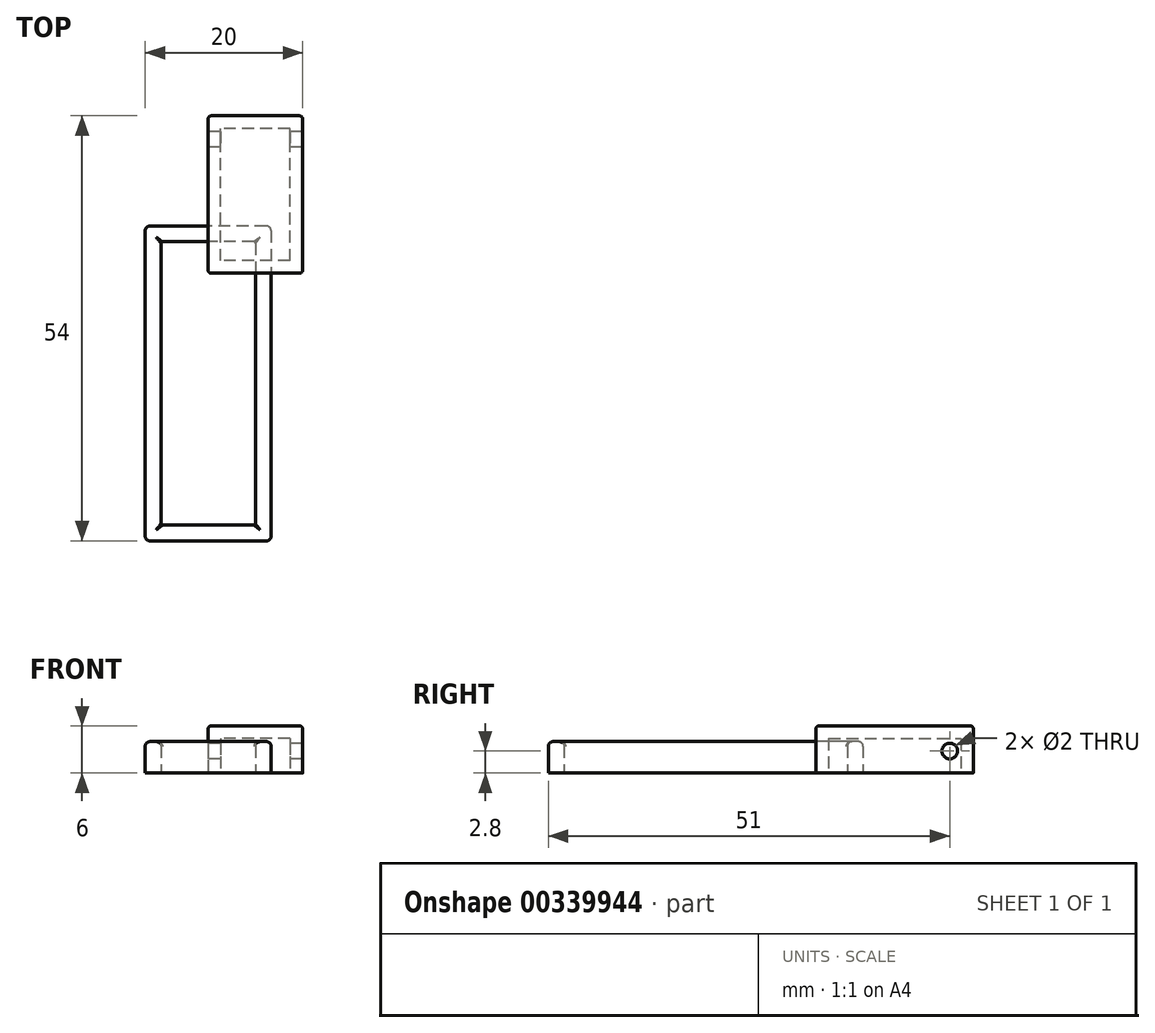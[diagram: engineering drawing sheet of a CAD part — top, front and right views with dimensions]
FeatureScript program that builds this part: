
annotation { "Feature Type Name" : "Feature", "Feature Type Description" : "" }
export const myFeature = defineFeature(function(context is Context, id is Id, definition is map)
    precondition{}
    {
        {
            var Q0;
            Q0=qCreatedBy(makeId("Top.planeOp"),FACE);
            var sketch = newSketch(context, id + "F0", { "sketchPlane" : qUnion([Q0])});
            skLineSegment(sketch, "E0.bottom", {"start": v(6, -10) * mm, "end": v(-6, -10) * mm});
            skLineSegment(sketch, "E0.top", {"start": v(6, 10) * mm, "end": v(-6, 10) * mm});
            skLineSegment(sketch, "E0.left", {"start": v(6, -10) * mm, "end": v(6, 10) * mm});
            skLineSegment(sketch, "E0.right", {"start": v(-6, -10) * mm, "end": v(-6, 10) * mm});
            skPoint(sketch, "E0.middle", {"position": v(0, 0) * mm});
            skSolve(sketch);
        }
        {
            var Q0;
            Q0 = qSketchRegion(id + "F0", true);
            extrude(context, id + "F1", {"entities" : qUnion([Q0]), "depth" : 6 * mm});
        }
        {
            var Q0;
            Q0=makeQuery(id+"F1.opExtrude","CAP_FACE",FACE,{"disambiguationData":[OSD([sQuery(id+"F0.wireOp",EDGE,"E0.bottom"),sQuery(id+"F0.wireOp",EDGE,"E0.top"),sQuery(id+"F0.wireOp",EDGE,"E0.left"),sQuery(id+"F0.wireOp",EDGE,"E0.right")])],"isStart":true});
            shell(context, id + "F2", {"entities" : qUnion([Q0]), "thickness" : 1.6 * mm});
        }
        {
            var Q0;
            Q0=qCreatedBy(makeId("Top.planeOp"),FACE);
            var sketch = newSketch(context, id + "F3", { "sketchPlane" : qUnion([Q0])});
            skLineSegment(sketch, "E1.bottom", {"start": v(2, -4) * mm, "end": v(-14, -4) * mm});
            skLineSegment(sketch, "E1.top", {"start": v(2, -44) * mm, "end": v(-14, -44) * mm});
            skLineSegment(sketch, "E1.left", {"start": v(2, -4) * mm, "end": v(2, -44) * mm});
            skLineSegment(sketch, "E1.right", {"start": v(-14, -4) * mm, "end": v(-14, -44) * mm});
            skPoint(sketch, "E1.middle", {"position": v(-6, -24) * mm});
            skLineSegment(sketch, "E2.0", {"start": v(0, -6) * mm, "end": v(-12, -6) * mm});
            skLineSegment(sketch, "E2.1", {"start": v(0, -6) * mm, "end": v(0, -42) * mm});
            skLineSegment(sketch, "E2.2", {"start": v(0, -42) * mm, "end": v(-12, -42) * mm});
            skLineSegment(sketch, "E2.3", {"start": v(-12, -6) * mm, "end": v(-12, -42) * mm});
            skSolve(sketch);
        }
        {
            var Q0;
            Q0 = qSketchRegion(id + "F3", true);
            extrude(context, id + "F4", {"entities" : qUnion([Q0]), "depth" : 4 * mm, "hasSecondDirection" : true, "secondDirectionOppositeDirection" : false, "secondDirectionDepth" : 0 * mm});
        }
        {
            var Q0;
            Q0=makeQuery(id+"F1.opExtrude","CAP_FACE",FACE,{"disambiguationData":[OSD([sQuery(id+"F0.wireOp",EDGE,"E0.bottom"),sQuery(id+"F0.wireOp",EDGE,"E0.top"),sQuery(id+"F0.wireOp",EDGE,"E0.left"),sQuery(id+"F0.wireOp",EDGE,"E0.right")])],"isStart":false});
            var Q1;
            Q1=makeQuery(id+"F1.opExtrude","SWEPT_EDGE",EDGE,{"disambiguationData":[OSD([sQuery(id+"F0.wireOp",EDGE,"E0.top"),sQuery(id+"F0.wireOp",EDGE,"E0.right")])]});
            var Q2;
            Q2=makeQuery(id+"F1.opExtrude","SWEPT_EDGE",EDGE,{"disambiguationData":[OSD([sQuery(id+"F0.wireOp",EDGE,"E0.bottom"),sQuery(id+"F0.wireOp",EDGE,"E0.right")])]});
            var Q3;
            Q3=makeQuery(id+"F1.opExtrude","SWEPT_EDGE",EDGE,{"disambiguationData":[OSD([sQuery(id+"F0.wireOp",EDGE,"E0.bottom"),sQuery(id+"F0.wireOp",EDGE,"E0.left")])]});
            var Q4;
            Q4=makeQuery(id+"F1.opExtrude","SWEPT_EDGE",EDGE,{"disambiguationData":[OSD([sQuery(id+"F0.wireOp",EDGE,"E0.top"),sQuery(id+"F0.wireOp",EDGE,"E0.left")])]});
            fillet(context, id + "F5", {"entities" : qUnion([Q0, Q1, Q2, Q3, Q4]), "radius" : 0.4 * mm, "tangentPropagation" : true, "allowEdgeOverflow" : false});
        }
        {
            var Q0;
            Q0=makeQuery(id+"F4.opExtrude","CAP_FACE",FACE,{"disambiguationData":[OSD([sQuery(id+"F3.wireOp",EDGE,"E1.bottom"),sQuery(id+"F3.wireOp",EDGE,"E1.top"),sQuery(id+"F3.wireOp",EDGE,"E1.left"),sQuery(id+"F3.wireOp",EDGE,"E1.right"),sQuery(id+"F3.wireOp",EDGE,"E2.0"),sQuery(id+"F3.wireOp",EDGE,"E2.1"),sQuery(id+"F3.wireOp",EDGE,"E2.2"),sQuery(id+"F3.wireOp",EDGE,"E2.3")])],"isStart":false});
            var Q1;
            Q1=makeQuery(id+"F4.opExtrude","SWEPT_EDGE",EDGE,{"disambiguationData":[OSD([sQuery(id+"F3.wireOp",EDGE,"E1.bottom"),sQuery(id+"F3.wireOp",EDGE,"E1.right")])]});
            var Q2;
            Q2=makeQuery(id+"F4.opExtrude","SWEPT_EDGE",EDGE,{"disambiguationData":[OSD([sQuery(id+"F3.wireOp",EDGE,"E1.bottom"),sQuery(id+"F3.wireOp",EDGE,"E1.left")])]});
            var Q3;
            Q3=makeQuery(id+"F4.opExtrude","SWEPT_EDGE",EDGE,{"disambiguationData":[OSD([sQuery(id+"F3.wireOp",EDGE,"E1.top"),sQuery(id+"F3.wireOp",EDGE,"E1.left")])]});
            var Q4;
            Q4=makeQuery(id+"F4.opExtrude","SWEPT_EDGE",EDGE,{"disambiguationData":[OSD([sQuery(id+"F3.wireOp",EDGE,"E1.top"),sQuery(id+"F3.wireOp",EDGE,"E1.right")])]});
            fillet(context, id + "F6", {"entities" : qUnion([Q0, Q1, Q2, Q3, Q4]), "radius" : 0.6 * mm, "tangentPropagation" : true, "allowEdgeOverflow" : false});
        }
        {
            var Q0;
            Q0=makeQuery(id+"F4.opExtrude","SWEPT_EDGE",EDGE,{"disambiguationData":[OSD([sQuery(id+"F3.wireOp",EDGE,"E2.0"),sQuery(id+"F3.wireOp",EDGE,"E2.3")])]});
            var Q1;
            Q1=makeQuery(id+"F4.opExtrude","SWEPT_EDGE",EDGE,{"disambiguationData":[OSD([sQuery(id+"F3.wireOp",EDGE,"E2.0"),sQuery(id+"F3.wireOp",EDGE,"E2.1")])]});
            var Q2;
            Q2=makeQuery(id+"F4.opExtrude","SWEPT_EDGE",EDGE,{"disambiguationData":[OSD([sQuery(id+"F3.wireOp",EDGE,"E2.2"),sQuery(id+"F3.wireOp",EDGE,"E2.3")])]});
            var Q3;
            Q3=makeQuery(id+"F4.opExtrude","SWEPT_EDGE",EDGE,{"disambiguationData":[OSD([sQuery(id+"F3.wireOp",EDGE,"E2.1"),sQuery(id+"F3.wireOp",EDGE,"E2.2")])]});
            fillet(context, id + "F7", {"entities" : qUnion([Q0, Q1, Q2, Q3]), "radius" : 0.2 * mm, "tangentPropagation" : true, "allowEdgeOverflow" : false});
        }
        {
            var Q0;
            Q0=makeQuery(id+"F1.opExtrude","SWEPT_FACE",FACE,{"disambiguationData":[OSD([sQuery(id+"F0.wireOp",EDGE,"E0.right")])]});
            var sketch = newSketch(context, id + "F8", { "sketchPlane" : qUnion([Q0])});
            skCircle(sketch, "E3", {"center": v(-7, 2.8) * mm, "radius": 1 * mm});
            skPoint(sketch, "E3.centerSnap0", {"position": v(-9.6, 2.8) * mm});
            skSolve(sketch);
        }
        {
            var Q0;
            Q0 = qSketchRegion(id + "F8", true);
            extrude(context, id + "F9", {"entities" : qUnion([Q0]), "operationType" : NewBodyOperationType.REMOVE, "oppositeDirection" : true, "depth" : 25 * mm});
        }
    });
